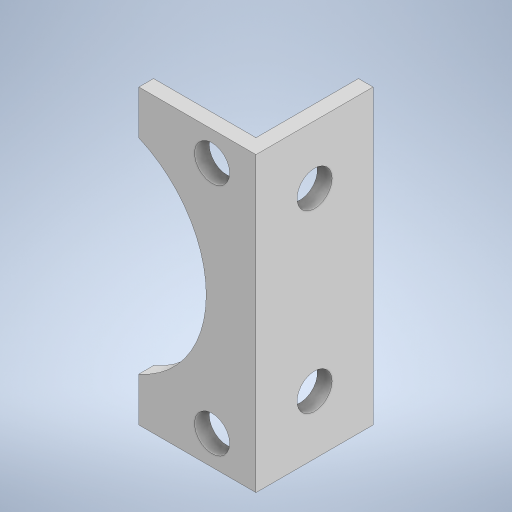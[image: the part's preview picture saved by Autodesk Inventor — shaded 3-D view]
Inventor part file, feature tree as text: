
AUTODESK INVENTOR PART (.ipt)
format: ipt  version: 2023 (Build 270158000, 158)  size: 249,856 bytes
history: native  units: in
note: dims shown in document units (in); Inventor stores cm internally (conversion verified against a paired STEP export)
features: extrude x3, sketch x3
ambient origin geometry x8: Origin, YZ Plane, XZ Plane, XY Plane, X Axis, Y Axis, Z Axis, Center Point
bodies: Solid1 (feature_tree)
feature tree (6):
  extrude  "Extrusion1"  Depth=0.125in
  extrude  "Extrusion2"  Depth=0.875in
  extrude  "Extrusion3"  Depth=2.5in
  sketch  "Sketch1"  dims[d0=1.0in d1=0.125in]
  sketch  "Sketch2"  dims[d2=0.875in d3=0.875in]
  sketch  "Sketch3"  dims[d4=2.5in d5=0.0in d6=0.25in d9=0.3in d10=0.3in d12=1.25in d13=2.5in d14=0.0in d18=2.5in d19=0.0in]
